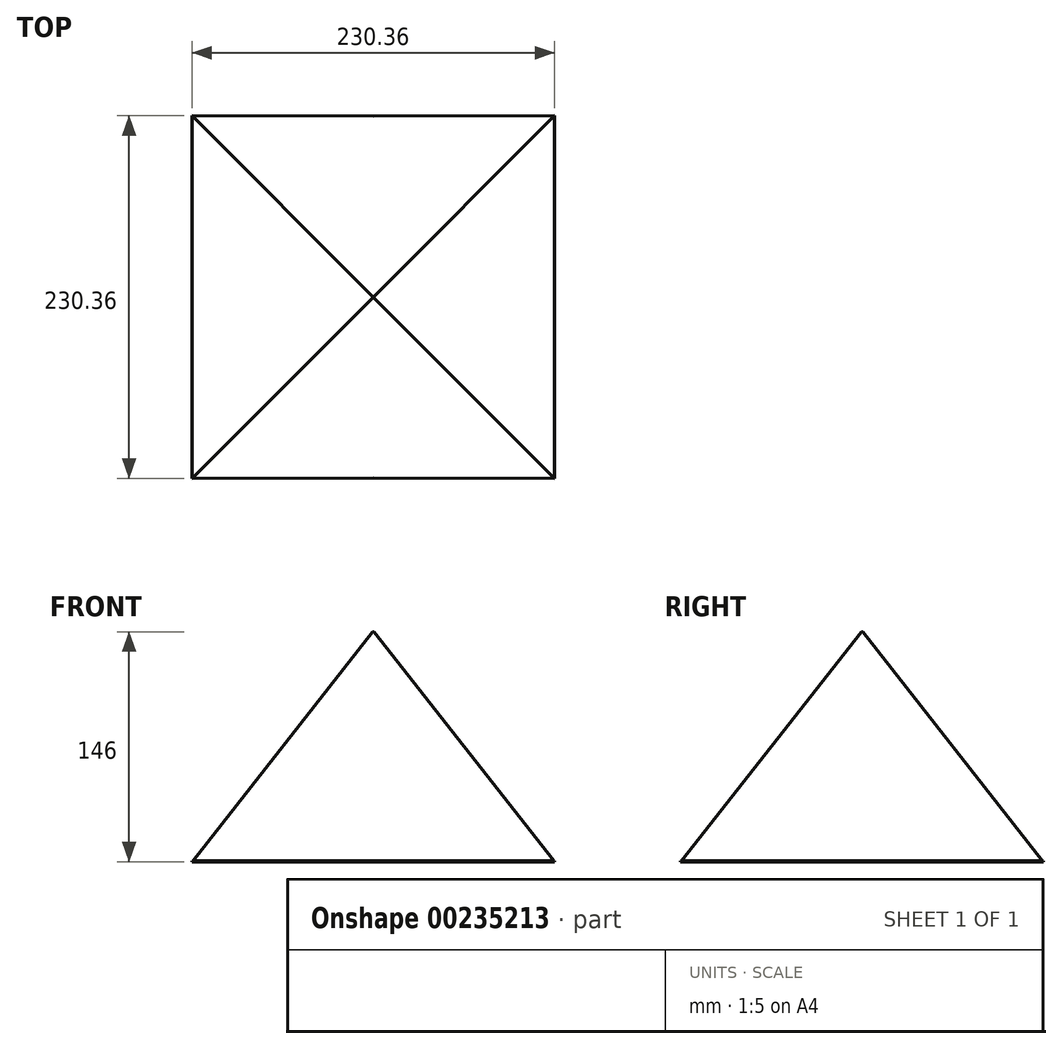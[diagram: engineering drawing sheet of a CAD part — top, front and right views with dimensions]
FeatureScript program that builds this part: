
annotation { "Feature Type Name" : "Feature", "Feature Type Description" : "" }
export const myFeature = defineFeature(function(context is Context, id is Id, definition is map)
    precondition{}
    {
        {
            var Q0;
            Q0=qCreatedBy(makeId("Top.planeOp"),FACE);
            var sketch = newSketch(context, id + "F0", { "sketchPlane" : qUnion([Q0])});
            skLineSegment(sketch, "E0", {"start": v(-115.18, -115.18) * mm, "end": v(115.18, 115.18) * mm, "construction": true});
            skLineSegment(sketch, "E1", {"start": v(-115.18, 115.18) * mm, "end": v(115.18, -115.18) * mm, "construction": true});
            skPoint(sketch, "E2", {"position": v(0, 0) * mm});
            skLineSegment(sketch, "E3", {"start": v(0, -115) * mm, "end": v(0, 115) * mm, "construction": true});
            skLineSegment(sketch, "E4", {"start": v(-115, 0) * mm, "end": v(115, 0) * mm, "construction": true});
            skLineSegment(sketch, "E5", {"start": v(-115.18, 115.18) * mm, "end": v(0, 115) * mm});
            skLineSegment(sketch, "E6", {"start": v(115.18, 115.18) * mm, "end": v(0, 115) * mm});
            skLineSegment(sketch, "E7", {"start": v(115.18, 115.18) * mm, "end": v(115, 0) * mm});
            skLineSegment(sketch, "E8", {"start": v(115, 0) * mm, "end": v(115.18, -115.18) * mm});
            skLineSegment(sketch, "E9", {"start": v(115.18, -115.18) * mm, "end": v(0, -115) * mm});
            skLineSegment(sketch, "E10", {"start": v(0, -115) * mm, "end": v(-115.18, -115.18) * mm});
            skLineSegment(sketch, "E11", {"start": v(-115.18, -115.18) * mm, "end": v(-115, 0) * mm});
            skLineSegment(sketch, "E12", {"start": v(-115, 0) * mm, "end": v(-115.18, 115.18) * mm});
            skSolve(sketch);
        }
        {
            var Q0;
            Q0=qCreatedBy(makeId("Top.planeOp"),FACE);
            cPlane(context, id + "F1", {"entities" : qUnion([Q0]), "cplaneType" : CPlaneType.OFFSET, "offset" : 146 * mm, "width" : 150 * mm, "height" : 150 * mm});
        }
        {
            var Q0;
            Q0=qCreatedBy(id+"F1.planeOp",FACE);
            var sketch = newSketch(context, id + "F2", { "sketchPlane" : qUnion([Q0])});
            skLineSegment(sketch, "E13.0", {"start": v(0.46, 0.46) * mm, "end": v(0.46, 0) * mm});
            skLineSegment(sketch, "E13.1", {"start": v(0.46, 0) * mm, "end": v(0.46, -0.46) * mm});
            skLineSegment(sketch, "E13.2", {"start": v(0.46, 0.46) * mm, "end": v(0, 0.46) * mm});
            skLineSegment(sketch, "E13.3", {"start": v(0.46, -0.46) * mm, "end": v(0, -0.46) * mm});
            skLineSegment(sketch, "E13.4", {"start": v(-0.46, 0.46) * mm, "end": v(0, 0.46) * mm});
            skLineSegment(sketch, "E13.5", {"start": v(-0.46, 0) * mm, "end": v(-0.46, 0.46) * mm});
            skLineSegment(sketch, "E13.6", {"start": v(-0.46, -0.46) * mm, "end": v(-0.46, 0) * mm});
            skLineSegment(sketch, "E13.7", {"start": v(0, -0.46) * mm, "end": v(-0.46, -0.46) * mm});
            skSolve(sketch);
        }
        {
            var Q0;
            Q0=makeQuery(id+"F2.imprint","IMPRINT",FACE,{"disambiguationData":[TD([[makeQuery(id+"F2.imprint","IMPRINT",EDGE,{"derivedFrom":sQuery(id+"F2.wireOp",EDGE,"E13.0")}),-1.0]])]});
            var Q1;
            Q1=makeQuery(id+"F0.imprint","IMPRINT",FACE,{"disambiguationData":[TD([[makeQuery(id+"F0.imprint","IMPRINT",EDGE,{"derivedFrom":sQuery(id+"F0.wireOp",EDGE,"E5")}),-1.0]])]});
            loft(context, id + "F3", {"sheetProfilesArray" : [{ "sheetProfileEntities" : qUnion([Q0]) }, { "sheetProfileEntities" : qUnion([Q1]) }]});
        }
        {
            var Q0;
            Q0 = qSketchRegion(id + "F0", true);
            extrude(context, id + "F4", {"entities" : qUnion([Q0]), "depth" : (146 / 210) * mm});
        }
    });
